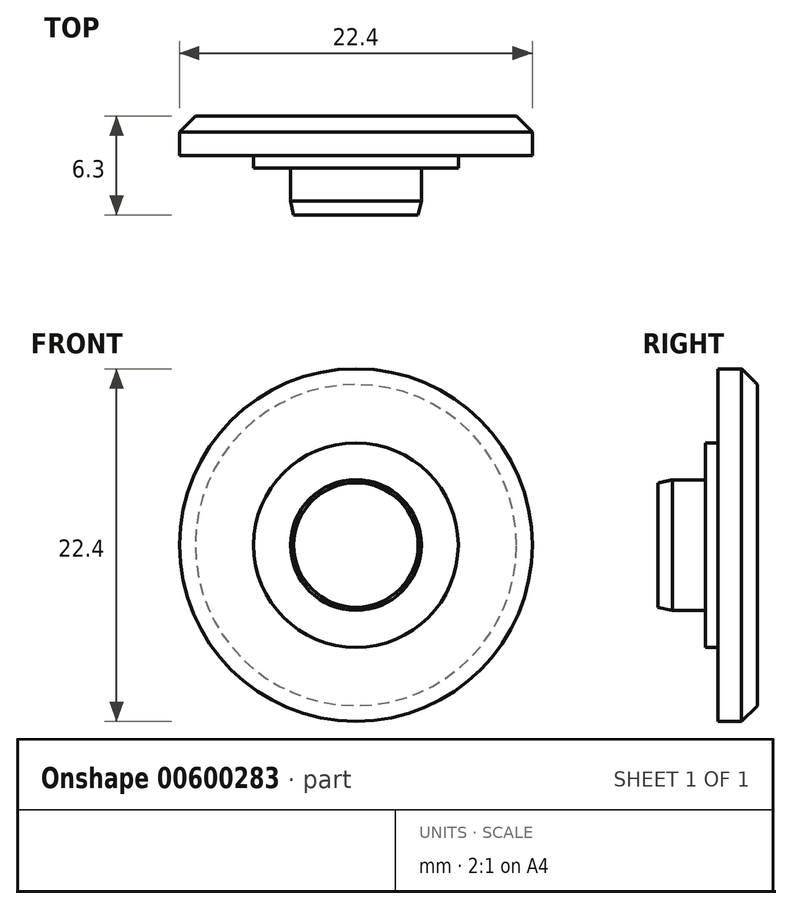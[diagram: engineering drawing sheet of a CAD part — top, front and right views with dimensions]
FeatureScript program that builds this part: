
annotation { "Feature Type Name" : "Feature", "Feature Type Description" : "" }
export const myFeature = defineFeature(function(context is Context, id is Id, definition is map)
    precondition{}
    {
        {
            var Q0;
            Q0=qCreatedBy(makeId("Right.planeOp"),FACE);
            var sketch = newSketch(context, id + "F0", { "sketchPlane" : qUnion([Q0])});
            skLineSegment(sketch, "E0", {"start": v(-0.63, 0) * mm, "end": v(6.3, 0) * mm, "construction": true});
            skLineSegment(sketch, "E1", {"start": v(6.3, 0) * mm, "end": v(6.3, 11.2) * mm});
            skLineSegment(sketch, "E2", {"start": v(3, 6.5) * mm, "end": v(3, 4.15) * mm});
            skLineSegment(sketch, "E3", {"start": v(3, 6.5) * mm, "end": v(3.8, 6.5) * mm});
            skLineSegment(sketch, "E4", {"start": v(3.8, 6.5) * mm, "end": v(3.8, 11.2) * mm});
            skLineSegment(sketch, "E5", {"start": v(3.8, 11.2) * mm, "end": v(6.3, 11.2) * mm});
            skLineSegment(sketch, "E6", {"start": v(6.3, 0) * mm, "end": v(0, 0) * mm});
            skLineSegment(sketch, "E7", {"start": v(0, 0) * mm, "end": v(0, 3.95) * mm});
            skLineSegment(sketch, "E8", {"start": v(0.9, 4.15) * mm, "end": v(3, 4.15) * mm});
            skLineSegment(sketch, "E9", {"start": v(0, 3.95) * mm, "end": v(0.9, 4.15) * mm});
            skSolve(sketch);
        }
        {
            var Q0;
            Q0 = qSketchRegion(id + "F0", true);
            var Q1;
            Q1=sQuery(id+"F0.wireOp",EDGE,"E6");
            revolve(context, id + "F1", {"entities" : qUnion([Q0]), "axis" : qUnion([Q1]), "revolveType" : RevolveType.FULL});
        }
        {
            var Q0;
            Q0=makeQuery(id+"F1.opRevolve","SWEPT_EDGE",EDGE,{"disambiguationData":[OSD([sQuery(id+"F0.wireOp",EDGE,"E1"),sQuery(id+"F0.wireOp",EDGE,"E5")])]});
            chamfer(context, id + "F2", {"entities" : qUnion([Q0]), "width" : 1 * mm, "tangentPropagation" : true});
        }
    });
